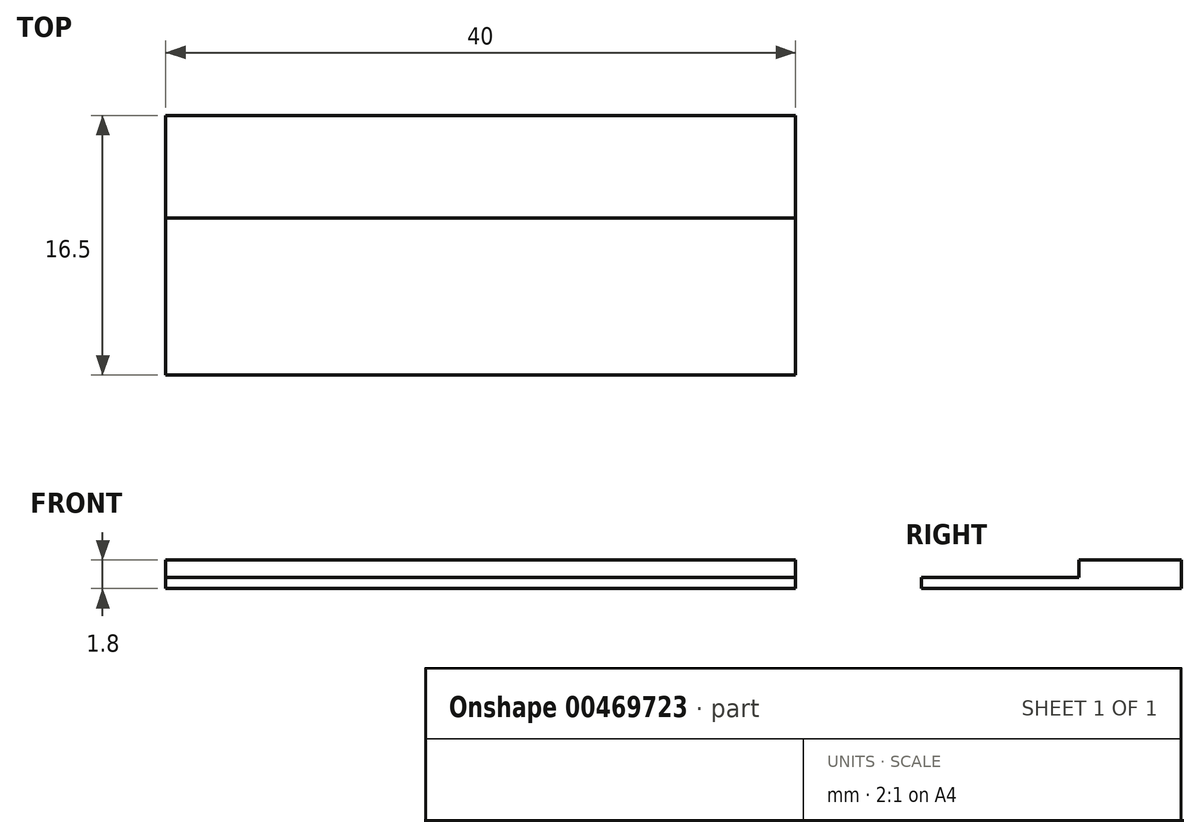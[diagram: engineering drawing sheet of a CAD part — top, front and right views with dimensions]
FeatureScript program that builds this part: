
annotation { "Feature Type Name" : "Feature", "Feature Type Description" : "" }
export const myFeature = defineFeature(function(context is Context, id is Id, definition is map)
    precondition{}
    {
        {
            var Q0;
            Q0=qCreatedBy(makeId("Top.planeOp"),FACE);
            var sketch = newSketch(context, id + "F0", { "sketchPlane" : qUnion([Q0])});
            skLineSegment(sketch, "E0", {"start": v(-36, 0) * mm, "end": v(0, 0) * mm});
            skLineSegment(sketch, "E1", {"start": v(-36, 1) * mm, "end": v(0, 1) * mm});
            skLineSegment(sketch, "E2.MirrorCS", {"start": v(-36, 2) * mm, "end": v(0, 2) * mm});
            skPoint(sketch, "E3", {"position": v(-31, 3.75) * mm});
            skPoint(sketch, "E4.MirrorP", {"position": v(-31, -1.75) * mm});
            skLineSegment(sketch, "E5", {"start": v(-31, 3.75) * mm, "end": v(-31, -1.75) * mm});
            skArc(sketch, "E6", {"start": v(-30.41, 3.47) * mm, "mid": v(-31, 3.75) * mm, "end": v(-31.59, 3.47) * mm});
            skLineSegment(sketch, "E7", {"start": v(-32.75, 2) * mm, "end": v(-31.59, 3.47) * mm});
            skPoint(sketch, "E8", {"position": v(-31.59, 3.47) * mm});
            skPoint(sketch, "E9", {"position": v(-30.41, 3.47) * mm});
            skLineSegment(sketch, "E10", {"start": v(-18, -5.38) * mm, "end": v(-18, 16.22) * mm});
            skFitSpline(sketch, "E11", {"points": [v(-35.93, 2) * mm, v(-35.23, 3.75) * mm, v(-34.53, 2) * mm, v(-34, 1) * mm, v(-34.07, 0) * mm, v(-35.93, 0) * mm, v(-36, 1) * mm, v(-35.93, 2) * mm]});
            skFitSpline(sketch, "E12.MirrorCS", {"points": [v(-35.93, 0) * mm, v(-35.23, -1.75) * mm, v(-34.53, 0) * mm, v(-34, 1) * mm, v(-34.07, 2) * mm, v(-35.93, 2) * mm, v(-36, 1) * mm, v(-35.93, 0) * mm]});
            skLineSegment(sketch, "E13.MirrorCS", {"start": v(-29.25, 2) * mm, "end": v(-30.41, 3.47) * mm});
            skLineSegment(sketch, "E14.MirrorCS", {"start": v(-32.75, 0) * mm, "end": v(-31.59, -1.47) * mm});
            skArc(sketch, "E15.MirrorCS", {"start": v(-30.41, -1.47) * mm, "mid": v(-31, -1.75) * mm, "end": v(-31.59, -1.47) * mm});
            skLineSegment(sketch, "E16.MirrorCS", {"start": v(-29.25, 0) * mm, "end": v(-30.41, -1.47) * mm});
            skFitSpline(sketch, "E17.MirrorCS", {"points": [v(-26.07, 2) * mm, v(-26.77, 3.75) * mm, v(-27.47, 2) * mm, v(-28, 1) * mm, v(-27.93, 0) * mm, v(-26.07, 0) * mm, v(-26, 1) * mm, v(-26.07, 2) * mm]});
            skFitSpline(sketch, "E18.MirrorCS", {"points": [v(-26.07, 0) * mm, v(-26.77, -1.75) * mm, v(-27.47, 0) * mm, v(-28, 1) * mm, v(-27.93, 2) * mm, v(-26.07, 2) * mm, v(-26, 1) * mm, v(-26.07, 0) * mm]});
            skFitSpline(sketch, "E19.MirrorCS", {"points": [v(-0.07, 2) * mm, v(-0.77, 3.75) * mm, v(-1.47, 2) * mm, v(-2, 1) * mm, v(-1.93, 0) * mm, v(-0.07, 0) * mm, v(0, 1) * mm, v(-0.07, 2) * mm]});
            skFitSpline(sketch, "E20.MirrorCS", {"points": [v(-0.07, 0) * mm, v(-0.77, -1.75) * mm, v(-1.47, 0) * mm, v(-2, 1) * mm, v(-1.93, 2) * mm, v(-0.07, 2) * mm, v(0, 1) * mm, v(-0.07, 0) * mm]});
            skLineSegment(sketch, "E21.MirrorCS", {"start": v(-3.25, 2) * mm, "end": v(-4.41, 3.47) * mm});
            skArc(sketch, "E22.MirrorCS", {"start": v(-5.59, 3.47) * mm, "mid": v(-5, 3.75) * mm, "end": v(-4.41, 3.47) * mm});
            skArc(sketch, "E23.MirrorCS", {"start": v(-5.59, -1.47) * mm, "mid": v(-5, -1.75) * mm, "end": v(-4.41, -1.47) * mm});
            skLineSegment(sketch, "E24.MirrorCS", {"start": v(-3.25, 0) * mm, "end": v(-4.41, -1.47) * mm});
            skLineSegment(sketch, "E25.MirrorCS", {"start": v(-6.75, 2) * mm, "end": v(-5.59, 3.47) * mm});
            skLineSegment(sketch, "E26.MirrorCS", {"start": v(-6.75, 0) * mm, "end": v(-5.59, -1.47) * mm});
            skFitSpline(sketch, "E27.MirrorCS", {"points": [v(-9.93, 2) * mm, v(-9.23, 3.75) * mm, v(-8.53, 2) * mm, v(-8, 1) * mm, v(-8.07, 0) * mm, v(-9.93, 0) * mm, v(-10, 1) * mm, v(-9.93, 2) * mm]});
            skFitSpline(sketch, "E28.MirrorCS", {"points": [v(-9.93, 0) * mm, v(-9.23, -1.75) * mm, v(-8.53, 0) * mm, v(-8, 1) * mm, v(-8.07, 2) * mm, v(-9.93, 2) * mm, v(-10, 1) * mm, v(-9.93, 0) * mm]});
            skSolve(sketch);
        }
        {
            var Q0;
            Q0=makeQuery(id+"F0YrUF3EvSyvHAe_0.opExtrude","CAP_FACE",FACE,{"disambiguationData":[OSD([sQuery(id+"F0.wireOp",EDGE,"E0"),sQuery(id+"F0.wireOp",EDGE,"E2.MirrorCS"),sQuery(id+"F0.wireOp",EDGE,"E6"),sQuery(id+"F0.wireOp",EDGE,"E7"),sQuery(id+"F0.wireOp",EDGE,"E11"),sQuery(id+"F0.wireOp",EDGE,"E12.MirrorCS"),sQuery(id+"F0.wireOp",EDGE,"E13.MirrorCS"),sQuery(id+"F0.wireOp",EDGE,"E14.MirrorCS"),sQuery(id+"F0.wireOp",EDGE,"E15.MirrorCS"),sQuery(id+"F0.wireOp",EDGE,"E16.MirrorCS"),sQuery(id+"F0.wireOp",EDGE,"E17.MirrorCS"),sQuery(id+"F0.wireOp",EDGE,"E18.MirrorCS"),sQuery(id+"F0.wireOp",EDGE,"E19.MirrorCS"),sQuery(id+"F0.wireOp",EDGE,"E20.MirrorCS"),sQuery(id+"F0.wireOp",EDGE,"E21.MirrorCS"),sQuery(id+"F0.wireOp",EDGE,"E22.MirrorCS"),sQuery(id+"F0.wireOp",EDGE,"E23.MirrorCS"),sQuery(id+"F0.wireOp",EDGE,"E24.MirrorCS"),sQuery(id+"F0.wireOp",EDGE,"E25.MirrorCS"),sQuery(id+"F0.wireOp",EDGE,"E26.MirrorCS"),sQuery(id+"F0.wireOp",EDGE,"E27.MirrorCS"),sQuery(id+"F0.wireOp",EDGE,"E28.MirrorCS")])],"isStart":true});
            var sketch = newSketch(context, id + "F1", { "sketchPlane" : qUnion([Q0])});
            skLineSegment(sketch, "E29", {"start": v(-39.5, -7.45) * mm, "end": v(3.5, -7.45) * mm});
            skLineSegment(sketch, "E30", {"start": v(-39.5, 9.55) * mm, "end": v(3.5, 9.55) * mm});
            skLineSegment(sketch, "E31", {"start": v(-39.5, 9.55) * mm, "end": v(-39.5, -7.45) * mm});
            skLineSegment(sketch, "E32", {"start": v(3.5, 9.55) * mm, "end": v(3.5, -7.45) * mm});
            skLineSegment(sketch, "E33", {"start": v(7.66, -11.25) * mm, "end": v(103.5, -11.25) * mm});
            skArc(sketch, "E34", {"start": v(7.66, -11.25) * mm, "mid": v(4.84, -10.15) * mm, "end": v(3.5, -7.45) * mm});
            skLineSegment(sketch, "E35", {"start": v(-39.5, 9.55) * mm, "end": v(-39.5, 13.55) * mm});
            skLineSegment(sketch, "E36", {"start": v(-39.5, 13.55) * mm, "end": v(103.5, 13.55) * mm});
            skLineSegment(sketch, "E37", {"start": v(103.5, -11.25) * mm, "end": v(103.5, 13.55) * mm});
            skLineSegment(sketch, "E38", {"start": v(-39.5, 13.55) * mm, "end": v(-43.8, 13.55) * mm});
            skLineSegment(sketch, "E39", {"start": v(-43.8, 13.55) * mm, "end": v(-43.8, -3.45) * mm});
            skArc(sketch, "E40", {"start": v(-43.8, -3.45) * mm, "mid": v(-42.52, -6.39) * mm, "end": v(-39.5, -7.45) * mm});
            skSolve(sketch);
        }
        {
            var Q0;
            Q0=makeQuery(id+"FhWCH0Bl1D4JLWu_1.opExtrude","CAP_FACE",FACE,{"disambiguationData":[OSD([sQuery(id+"F1.wireOp",EDGE,"E30"),sQuery(id+"F1.wireOp",EDGE,"E31"),sQuery(id+"F1.wireOp",EDGE,"E32"),sQuery(id+"F1.wireOp",EDGE,"E33"),sQuery(id+"F1.wireOp",EDGE,"E34"),sQuery(id+"F1.wireOp",EDGE,"E36"),sQuery(id+"F1.wireOp",EDGE,"E37"),sQuery(id+"F1.wireOp",EDGE,"E38"),sQuery(id+"F1.wireOp",EDGE,"E39"),sQuery(id+"F1.wireOp",EDGE,"E40")])],"isStart":false});
            var sketch = newSketch(context, id + "F2", { "sketchPlane" : qUnion([Q0])});
            skLineSegment(sketch, "E41.bottom", {"start": v(3.5, -9.55) * mm, "end": v(-39.5, -9.55) * mm});
            skLineSegment(sketch, "E41.top", {"start": v(3.5, 0.45) * mm, "end": v(-39.5, 0.45) * mm});
            skLineSegment(sketch, "E41.left", {"start": v(3.5, -9.55) * mm, "end": v(3.5, 0.45) * mm});
            skLineSegment(sketch, "E41.right", {"start": v(-39.5, -9.55) * mm, "end": v(-39.5, 0.45) * mm});
            skSolve(sketch);
        }
        {
            var Q0;
            Q0=qCreatedBy(makeId("Top.planeOp"),FACE);
            var sketch = newSketch(context, id + "F3", { "sketchPlane" : qUnion([Q0])});
            skLineSegment(sketch, "E42", {"start": v(3.5, 7.45) * mm, "end": v(-39.5, 7.45) * mm});
            skPoint(sketch, "E43.endSnap0", {"position": v(-39.5, 3.95) * mm});
            skLineSegment(sketch, "E44.bottom", {"start": v(-1.49, 9.8) * mm, "end": v(-41.49, 9.8) * mm});
            skLineSegment(sketch, "E44.top", {"start": v(-1.49, 26.3) * mm, "end": v(-41.49, 26.3) * mm});
            skLineSegment(sketch, "E44.left", {"start": v(-1.49, 9.8) * mm, "end": v(-1.49, 26.3) * mm});
            skLineSegment(sketch, "E44.right", {"start": v(-41.49, 9.8) * mm, "end": v(-41.49, 26.3) * mm});
            skLineSegment(sketch, "E45", {"start": v(-1.49, 19.8) * mm, "end": v(-41.49, 19.8) * mm});
            skSolve(sketch);
        }
        {
            var Q0;
            {var subQ0=sQuery(id+"F3.wireOp",EDGE,"E44.bottom");Q0=makeQuery(id+"F3.imprint","IMPRINT",FACE,{"disambiguationData":[TD([[makeQuery(id+"F3.imprint","IMPRINT",EDGE,{"derivedFrom":subQ0}),-1.0]])]});}
            extrude(context, id + "F4", {"entities" : qUnion([Q0]), "offsetDistance" : 25 * mm, "depth" : .7 * mm});
        }
        {
            var Q0;
            {var subQ0=sQuery(id+"F3.wireOp",EDGE,"E44.top");Q0=makeQuery(id+"F3.imprint","IMPRINT",FACE,{"disambiguationData":[TD([[makeQuery(id+"F3.imprint","IMPRINT",EDGE,{"derivedFrom":subQ0}),1.0]])]});}
            extrude(context, id + "F5", {"entities" : qUnion([Q0]), "operationType" : NewBodyOperationType.ADD, "depth" : 1.8 * mm});
        }
    });
